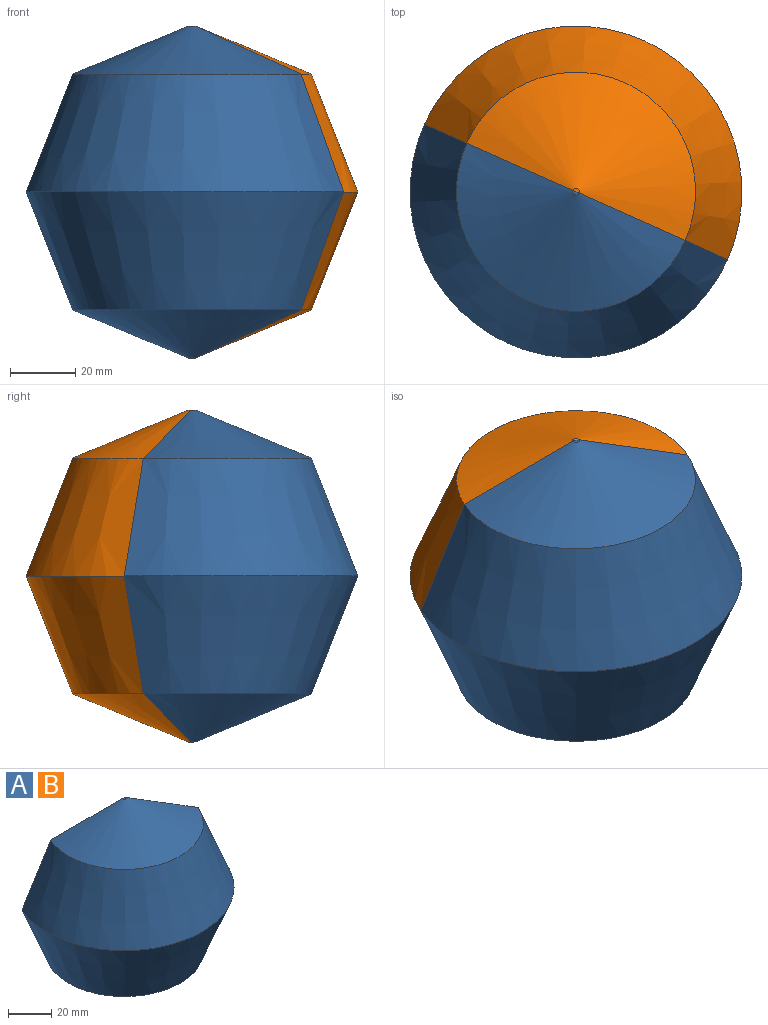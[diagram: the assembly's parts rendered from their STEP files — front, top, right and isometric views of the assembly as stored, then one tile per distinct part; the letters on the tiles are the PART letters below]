
ASSEMBLY  parts=2 mates=1
PART A: 7 faces, bbox 97.2x71.5x101.6 mm
  f0: plane 101.6x92.78mm, normal (0.41,0.91,0), area 7412.8mm2, adj f1,f2,f3,f4,f5,f6
  f1: plane 1.97x1.45mm, normal (0,0,1), area 1.7mm2, adj f0,f6
  f2: plane 1.97x1.45mm, normal (0,0,-1), area 1.7mm2, adj f0,f5
  f3: cone r=50.8mm half-angle=21.5deg, axis (0,0,1), area 5321.9mm2, adj f0,f4,f5
  f4: cone r=30.79mm half-angle=21.5deg, axis (0,0,-1), area 5321.9mm2, adj f0,f3,f6
  f5: cone r=1.03mm half-angle=67.5deg, axis (0,0,1), area 2274.7mm2, adj f0,f2,f3
  f6: cone r=1.03mm half-angle=67.5deg, axis (0,0,-1), area 2274.7mm2, adj f0,f1,f4
PART B: same geometry as A
PLACE A t=(1.31,39.73,-87.87)mm
PLACE B rot(axis=(0.91,-0.41,0),180deg) t=(1.31,39.73,13.73)mm
MATE fastened B.f0 <-> A.f0  axis (-0.41,-0.91,0) through (1.31,39.73,-37.07)mm
